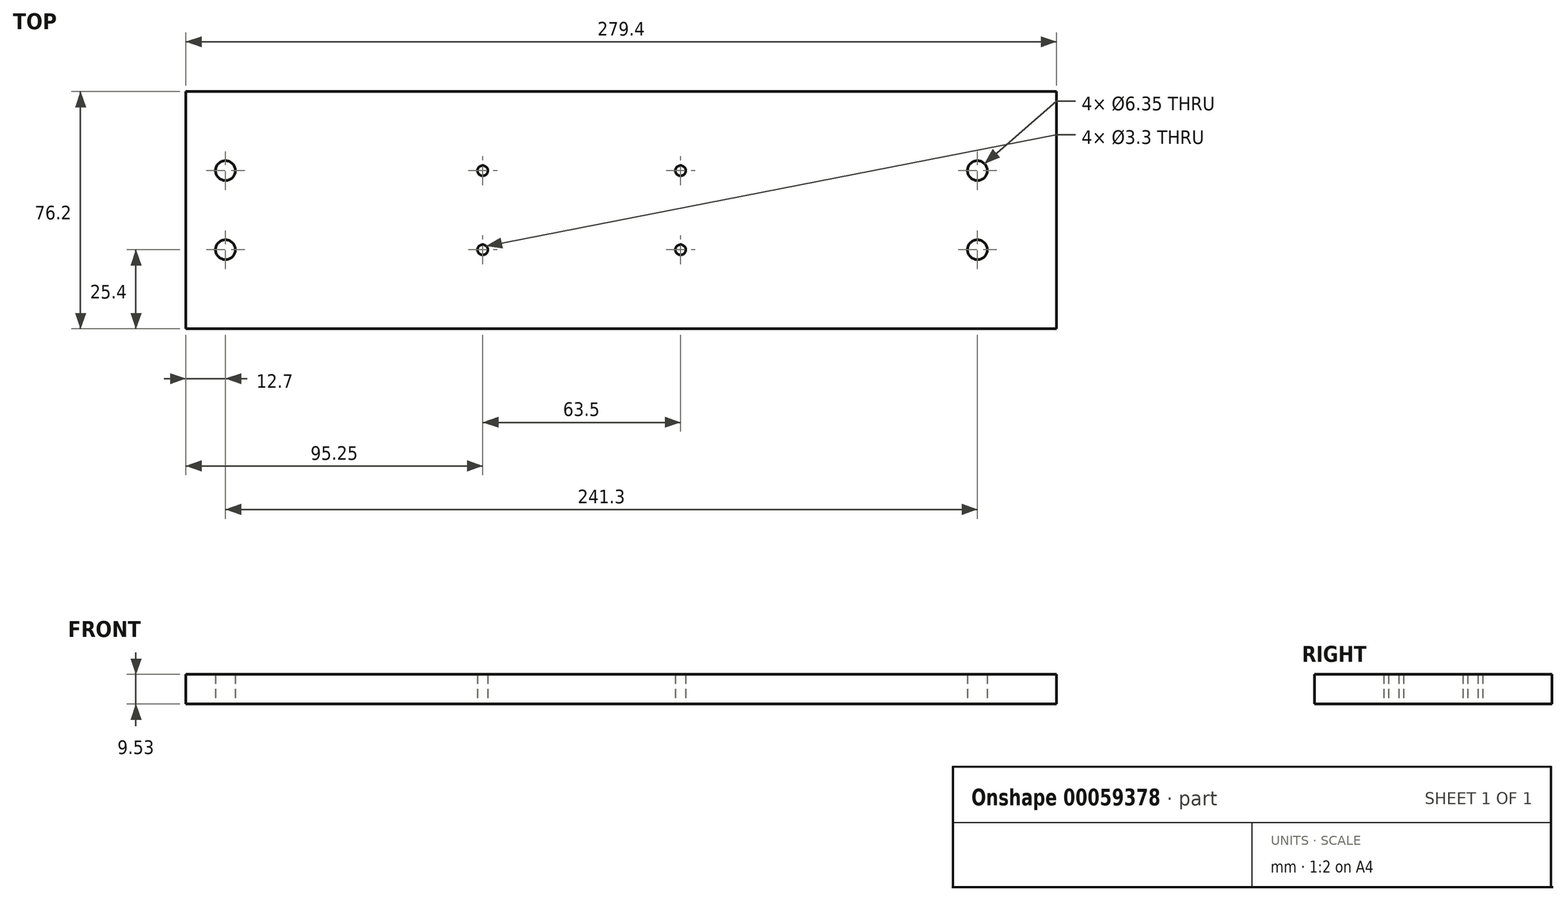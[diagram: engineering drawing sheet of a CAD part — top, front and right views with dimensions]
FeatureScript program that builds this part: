
annotation { "Feature Type Name" : "Feature", "Feature Type Description" : "" }
export const myFeature = defineFeature(function(context is Context, id is Id, definition is map)
    precondition{}
    {
        {
            var Q0;
            Q0=qCreatedBy(makeId("Top.planeOp"),FACE);
            var sketch = newSketch(context, id + "F0", { "sketchPlane" : qUnion([Q0])});
            skLineSegment(sketch, "E0.bottom", {"start": v(-152.4, 38.1) * mm, "end": v(127, 38.1) * mm});
            skLineSegment(sketch, "E0.top", {"start": v(-152.4, -38.1) * mm, "end": v(127, -38.1) * mm});
            skLineSegment(sketch, "E0.left", {"start": v(-152.4, 38.1) * mm, "end": v(-152.4, -38.1) * mm});
            skLineSegment(sketch, "E0.right", {"start": v(127, 38.1) * mm, "end": v(127, -38.1) * mm});
            skLineSegment(sketch, "E1", {"start": v(0, 0) * mm, "end": v(0, 58.03) * mm, "construction": true});
            skLineSegment(sketch, "E2", {"start": v(0, 0) * mm, "end": v(-114.76, 0) * mm, "construction": true});
            skCircle(sketch, "E3", {"center": v(-139.7, 12.7) * mm, "radius": 3.18 * mm});
            skCircle(sketch, "E4", {"center": v(-139.7, -12.7) * mm, "radius": 3.18 * mm});
            skCircle(sketch, "E5", {"center": v(-57.15, 12.7) * mm, "radius": 1.65 * mm});
            skCircle(sketch, "E6", {"center": v(-57.15, -12.7) * mm, "radius": 1.65 * mm});
            skCircle(sketch, "E7", {"center": v(6.35, 12.7) * mm, "radius": 1.65 * mm});
            skCircle(sketch, "E8", {"center": v(6.35, -12.7) * mm, "radius": 1.65 * mm});
            skCircle(sketch, "E9", {"center": v(101.6, 12.7) * mm, "radius": 3.18 * mm});
            skCircle(sketch, "E10", {"center": v(101.6, -12.7) * mm, "radius": 3.18 * mm});
            skSolve(sketch);
        }
        {
            var Q0;
            Q0 = qSketchRegion(id + "F0", true);
            extrude(context, id + "F1", {"entities" : qUnion([Q0]), "depth" : 9.52 * mm});
        }
    });
